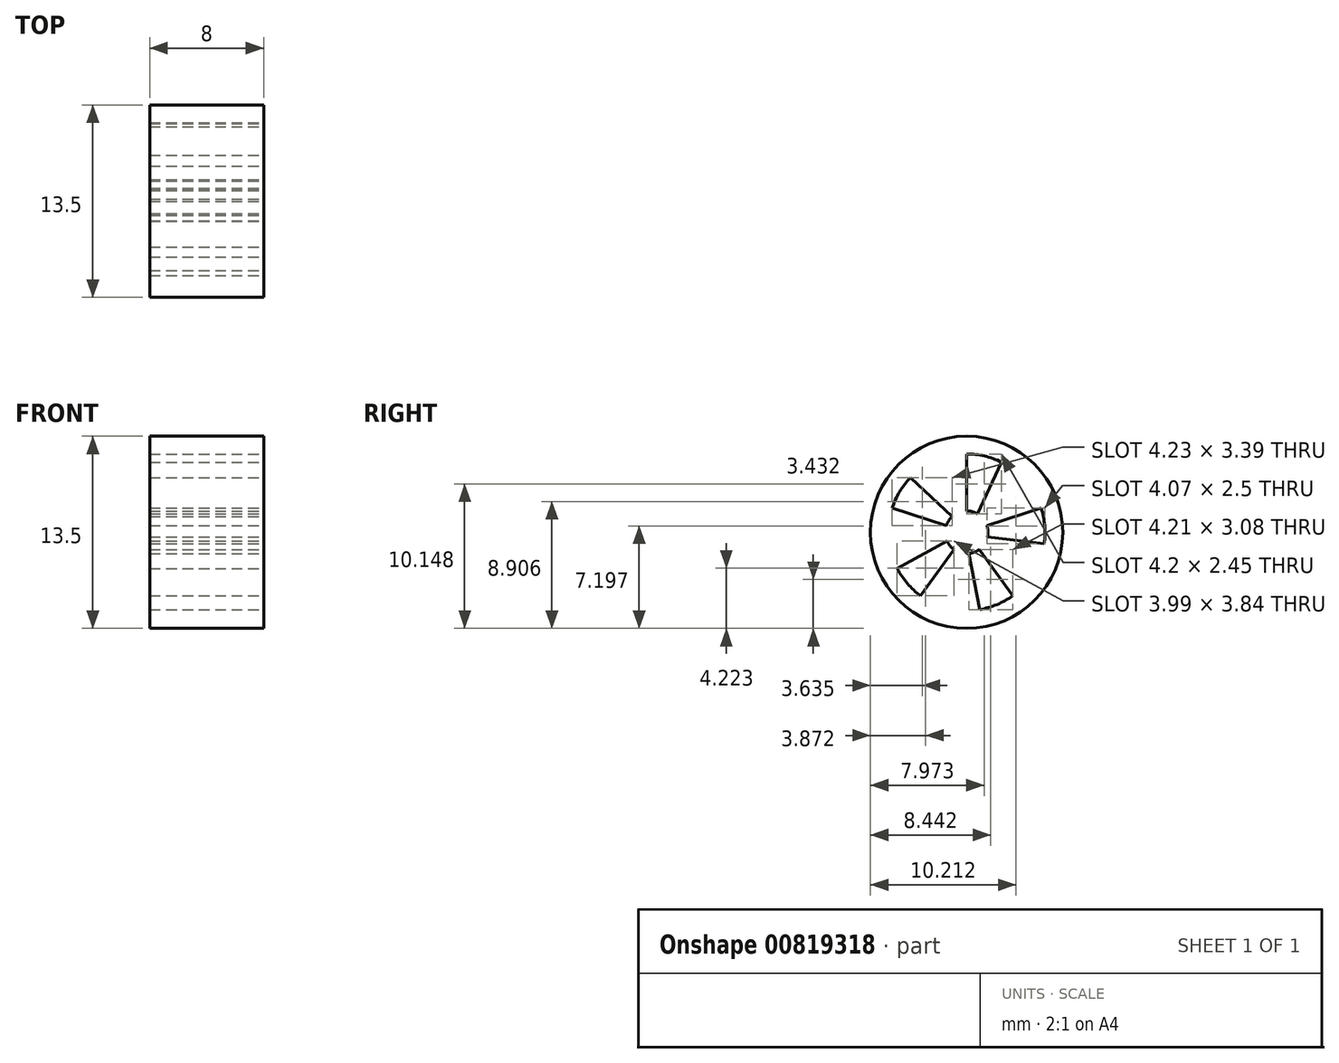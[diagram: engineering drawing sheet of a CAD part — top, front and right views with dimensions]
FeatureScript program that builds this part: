
annotation { "Feature Type Name" : "Feature", "Feature Type Description" : "" }
export const myFeature = defineFeature(function(context is Context, id is Id, definition is map)
    precondition{}
    {
        {
            var Q0;
            Q0=qCreatedBy(makeId("Right.planeOp"),FACE);
            var sketch = newSketch(context, id + "F0", { "sketchPlane" : qUnion([Q0])});
            skCircle(sketch, "E0", {"center": v(0, 0) * mm, "radius": 6.75 * mm});
            skSolve(sketch);
        }
        {
            var Q0;
            Q0=makeQuery(id+"F0.imprint","IMPRINT",FACE,{"disambiguationData":[TD([[makeQuery(id+"F0.imprint","IMPRINT",EDGE,{"derivedFrom":sQuery(id+"F0.wireOp",EDGE,"E0")}),1.0]])]});
            extrude(context, id + "F1", {"entities" : qUnion([Q0]), "depth" : 8 * mm, "offsetDistance" : 25 * mm});
        }
        {
            var Q0;
            Q0=makeQuery(id+"F1.opExtrude","CAP_FACE",FACE,{"disambiguationData":[OSD([sQuery(id+"F0.wireOp",EDGE,"E0")])],"isStart":false});
            var sketch = newSketch(context, id + "F2", { "sketchPlane" : qUnion([Q0])});
            skCircle(sketch, "E1", {"center": v(0, 0) * mm, "radius": 1.5 * mm});
            skCircle(sketch, "E2", {"center": v(0, 0) * mm, "radius": 5.5 * mm});
            skLineSegment(sketch, "E3", {"start": v(0, 1.5) * mm, "end": v(0, 5.5) * mm});
            skLineSegment(sketch, "E4", {"start": v(0.75, 1.3) * mm, "end": v(2.45, 4.93) * mm});
            skLineSegment(sketch, "E5.1.0", {"start": v(-1.43, 0.46) * mm, "end": v(-5.23, 1.7) * mm});
            skLineSegment(sketch, "E5.1.1", {"start": v(-1, 1.12) * mm, "end": v(-3.93, 3.85) * mm});
            skLineSegment(sketch, "E5.2.0", {"start": v(-0.88, -1.21) * mm, "end": v(-3.23, -4.45) * mm});
            skLineSegment(sketch, "E5.2.1", {"start": v(-1.37, -0.6) * mm, "end": v(-4.87, -2.55) * mm});
            skLineSegment(sketch, "E5.3.0", {"start": v(0.88, -1.21) * mm, "end": v(3.23, -4.45) * mm});
            skLineSegment(sketch, "E5.3.1", {"start": v(0.15, -1.5) * mm, "end": v(0.92, -5.42) * mm});
            skLineSegment(sketch, "E5.4.0", {"start": v(1.43, 0.46) * mm, "end": v(5.23, 1.7) * mm});
            skLineSegment(sketch, "E5.4.1", {"start": v(1.47, -0.32) * mm, "end": v(5.44, -0.8) * mm});
            skSolve(sketch);
        }
        {
            var Q0;
            {var subQ0=sQuery(id+"F2.wireOp",EDGE,"E5.1.0");Q0=makeQuery(id+"F2.imprint","IMPRINT",FACE,{"disambiguationData":[TD([[makeQuery(id+"F2.imprint","IMPRINT",EDGE,{"derivedFrom":subQ0}),-1.0]])]});}
            var Q1;
            {var subQ0=sQuery(id+"F2.wireOp",EDGE,"E5.2.0");Q1=makeQuery(id+"F2.imprint","IMPRINT",FACE,{"disambiguationData":[TD([[makeQuery(id+"F2.imprint","IMPRINT",EDGE,{"derivedFrom":subQ0}),-1.0]])]});}
            var Q2;
            {var subQ0=sQuery(id+"F2.wireOp",EDGE,"E3");Q2=makeQuery(id+"F2.imprint","IMPRINT",FACE,{"disambiguationData":[TD([[makeQuery(id+"F2.imprint","IMPRINT",EDGE,{"derivedFrom":subQ0}),-1.0]])]});}
            var Q3;
            {var subQ0=sQuery(id+"F2.wireOp",EDGE,"E5.3.0");Q3=makeQuery(id+"F2.imprint","IMPRINT",FACE,{"disambiguationData":[TD([[makeQuery(id+"F2.imprint","IMPRINT",EDGE,{"derivedFrom":subQ0}),-1.0]])]});}
            var Q4;
            {var subQ0=sQuery(id+"F2.wireOp",EDGE,"E5.4.0");Q4=makeQuery(id+"F2.imprint","IMPRINT",FACE,{"disambiguationData":[TD([[makeQuery(id+"F2.imprint","IMPRINT",EDGE,{"derivedFrom":subQ0}),-1.0]])]});}
            extrude(context, id + "F3", {"entities" : qUnion([Q0, Q1, Q2, Q3, Q4]), "operationType" : NewBodyOperationType.REMOVE, "endBound" : BoundingType.THROUGH_ALL, "oppositeDirection" : true, "depth" : 25 * mm, "offsetDistance" : 25 * mm});
        }
    });
